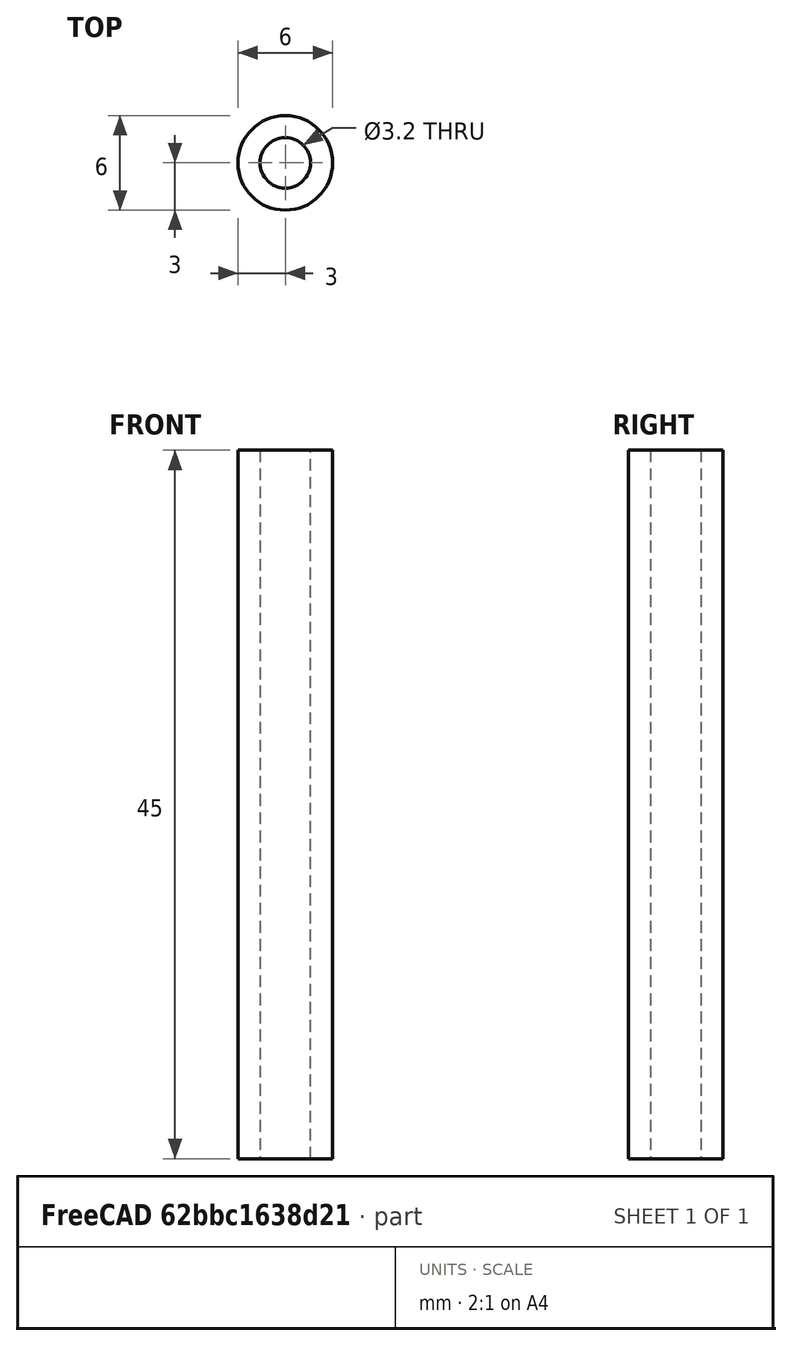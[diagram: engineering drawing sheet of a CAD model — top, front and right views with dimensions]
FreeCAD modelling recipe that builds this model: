
FCSTD DOCUMENT  (FreeCAD 1.0R39109 (Git))
Label: 45mm_spacer
License: All rights reserved
LicenseURL: https://en.wikipedia.org/wiki/All_rights_reserved
objects: Sketcher::SketchObject×1, PartDesign::Pad×1, PartDesign::Body×1
note: 6 computed .brp shape members not serialized (recipe doc carries the construction recipe); baked Part::Feature solids carry a one-line shape summary decoded from their .brp

FEATURE [Sketcher::SketchObject] Sketch
  ArcFitTolerance = 1e-06
  AttachmentSupport = -> [XY_Plane]
  FullyConstrained = true
  MakeInternals = false
  MapMode = 5
  sketch-geometry (2):
    g0: Circle CenterX=0 CenterY=0 CenterZ=0 NormalX=0 NormalY=0 NormalZ=1 AngleXU=0 Radius=1.6
    g1: Circle CenterX=0 CenterY=0 CenterZ=0 NormalX=0 NormalY=0 NormalZ=1 AngleXU=0 Radius=3
  constraints (4):
    c: Coincident(g0,g-1)
    c: Coincident(g1,g0)
    c: Diameter(g0) = 3.2
    c: Diameter(g1) = 6
FEATURE [PartDesign::Pad] Pad
  Direction = (0,0,1)
  Length = 45
  Length2 = 10
  Profile = -> Sketch
  ReferenceAxis = -> Sketch [N_Axis]
  Refine = true
  Suppressed = false
  Type = 0
FEATURE [PartDesign::Body] Body
  AllowCompound = false
  Group = -> [Sketch,Pad]
  Origin = -> Origin
  Tip = -> Pad
